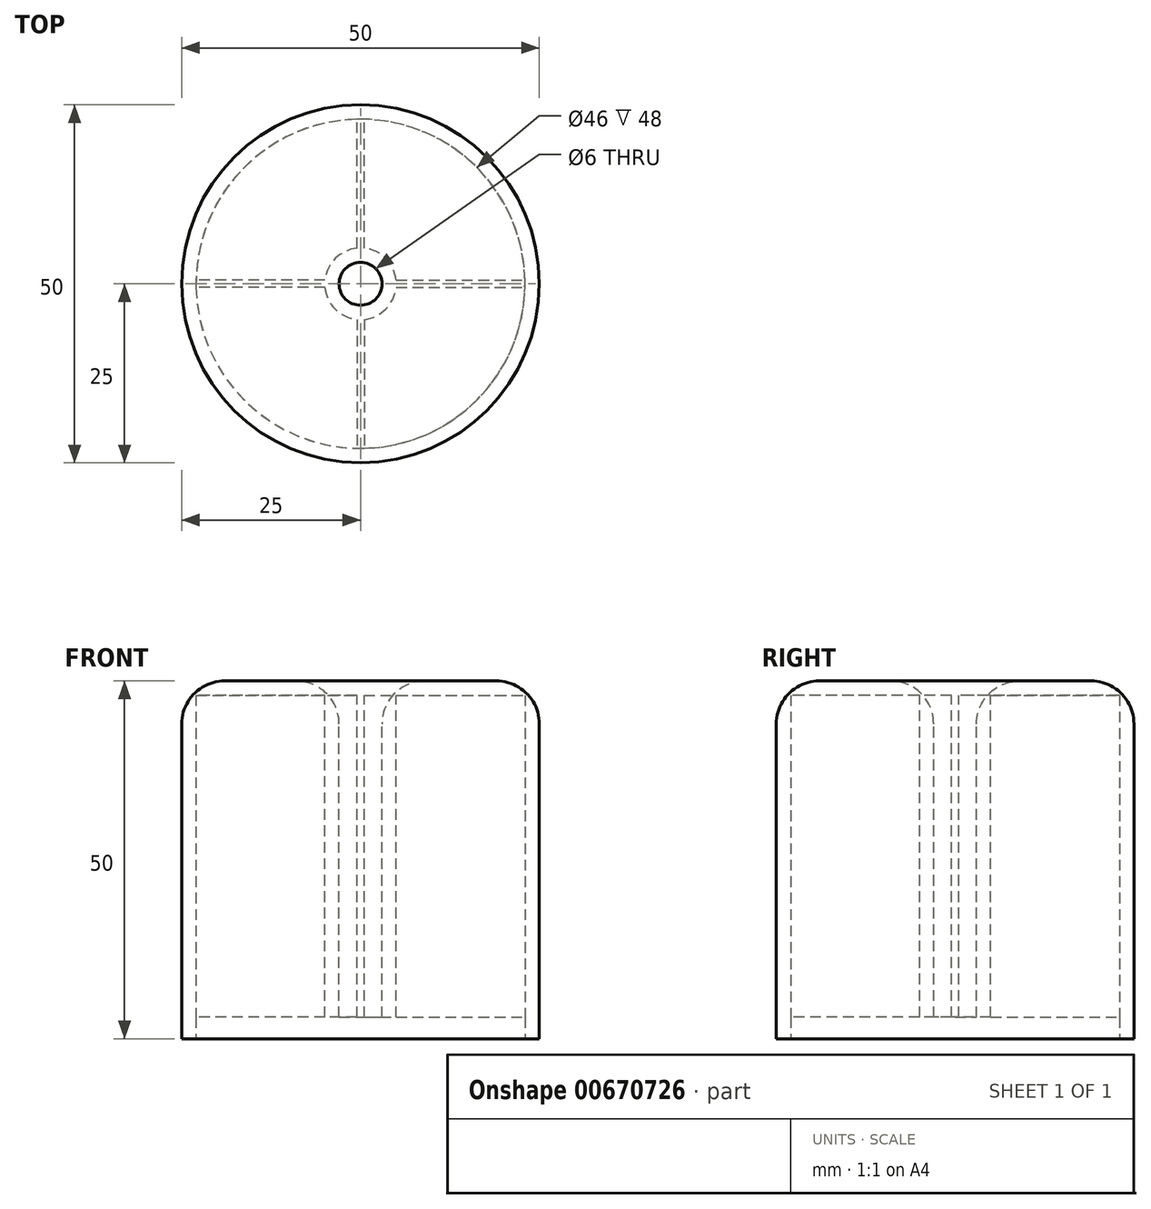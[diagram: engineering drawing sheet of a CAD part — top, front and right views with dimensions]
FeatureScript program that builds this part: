
annotation { "Feature Type Name" : "Feature", "Feature Type Description" : "" }
export const myFeature = defineFeature(function(context is Context, id is Id, definition is map)
    precondition{}
    {
        {
            var Q0;
            Q0=qCreatedBy(makeId("Top.planeOp"),FACE);
            var sketch = newSketch(context, id + "F0", { "sketchPlane" : qUnion([Q0])});
            skCircle(sketch, "E0", {"center": v(0, 0) * mm, "radius": 25 * mm});
            skSolve(sketch);
        }
        {
            var Q0;
            Q0 = qSketchRegion(id + "F0", true);
            extrude(context, id + "F1", {"entities" : qUnion([Q0]), "depth" : 50 * mm, "offsetDistance" : 25 * mm});
        }
        {
            var Q0;
            Q0=makeQuery(id+"F1.opExtrude","CAP_FACE",FACE,{"disambiguationData":[OSD([sQuery(id+"F0.wireOp",EDGE,"E0")])],"isStart":false});
            var sketch = newSketch(context, id + "F2", { "sketchPlane" : qUnion([Q0])});
            skCircle(sketch, "E1", {"center": v(0, 0) * mm, "radius": 3 * mm});
            skSolve(sketch);
        }
        {
            var Q0;
            Q0 = qSketchRegion(id + "F2", true);
            extrude(context, id + "F3", {"entities" : qUnion([Q0]), "operationType" : NewBodyOperationType.REMOVE, "oppositeDirection" : true, "depth" : 48 * mm, "offsetDistance" : 25 * mm});
        }
        {
            var Q0;
            Q0=makeQuery(id+"F1.opExtrude","CAP_FACE",FACE,{"disambiguationData":[OSD([sQuery(id+"F0.wireOp",EDGE,"E0")])],"isStart":true});
            shell(context, id + "F4", {"entities" : qUnion([Q0]), "thickness" : 2 * mm});
        }
        {
            var Q0;
            {var subQ0=sQuery(id+"F2.wireOp",EDGE,"E1");Q0=makeQuery(id+"F4.opShell","OFFSET_FACE",FACE,{"disambiguationData":[OSD([subQ0]),TDD([makeQuery(id+"F3.boolean.opBoolean","COPY",FACE,{"derivedFrom":makeQuery(id+"F3.opExtrude","CAP_FACE",FACE,{"disambiguationData":[OSD([subQ0])],"isStart":false})})])]});}
            var sketch = newSketch(context, id + "F5", { "sketchPlane" : qUnion([Q0])});
            skCircle(sketch, "E2.0", {"center": v(0, 0) * mm, "radius": 5 * mm});
            skSolve(sketch);
        }
        {
            var Q0;
            Q0 = qSketchRegion(id + "F5", true);
            extrude(context, id + "F6", {"entities" : qUnion([Q0]), "operationType" : NewBodyOperationType.REMOVE, "oppositeDirection" : true, "depth" : 3 * mm, "offsetDistance" : 25 * mm});
        }
        {
            var Q0;
            Q0=makeQuery(id+"F1.opExtrude","CAP_FACE",FACE,{"disambiguationData":[OSD([sQuery(id+"F0.wireOp",EDGE,"E0")])],"isStart":false});
            fillet(context, id + "F7", {"entities" : qUnion([Q0]), "radius" : 6 * mm, "tangentPropagation" : true, "allowEdgeOverflow" : false});
        }
        {
            var Q0;
            Q0=makeQuery(id+"F6.boolean.opBoolean","COPY",FACE,{"derivedFrom":makeQuery(id+"F6.opExtrude","CAP_FACE",FACE,{"disambiguationData":[OSD([sQuery(id+"F5.wireOp",EDGE,"E2.0")])],"isStart":false})});
            var sketch = newSketch(context, id + "F8", { "sketchPlane" : qUnion([Q0])});
            skLineSegment(sketch, "E3", {"start": v(0, 0) * mm, "end": v(25.2, 0) * mm, "construction": true});
            skLineSegment(sketch, "E4.0", {"start": v(3.98, -0.5) * mm, "end": v(23.8, -0.5) * mm});
            skLineSegment(sketch, "E5.0", {"start": v(3.98, 0.5) * mm, "end": v(23.8, 0.5) * mm});
            skLineSegment(sketch, "E6", {"start": v(3.98, 0.5) * mm, "end": v(3.98, -0.5) * mm});
            skLineSegment(sketch, "E7", {"start": v(23.8, 0.5) * mm, "end": v(23.8, -0.5) * mm});
            skPoint(sketch, "E8.orphan", {"position": v(25.2, -0.5) * mm});
            skSolve(sketch);
        }
        {
            var Q0;
            Q0 = qSketchRegion(id + "F8", true);
            extrude(context, id + "F9", {"entities" : qUnion([Q0]), "operationType" : NewBodyOperationType.ADD, "endBound" : BoundingType.UP_TO_NEXT, "oppositeDirection" : true, "depth" : 25 * mm, "offsetDistance" : 25 * mm});
        }
        {
            var Q0;
            Q0=makeQuery(id+"F1.opExtrude","SWEPT_BODY",BODY,{"disambiguationData":[OSD([sQuery(id+"F0.wireOp",EDGE,"E0")])]});
            var Q1;
            Q1=makeQuery(id+"F3.boolean.opBoolean","COPY",FACE,{"derivedFrom":makeQuery(id+"F3.opExtrude","SWEPT_FACE",FACE,{"disambiguationData":[OSD([sQuery(id+"F2.wireOp",EDGE,"E1")])]})});
            circularPattern(context, id + "F10", {"operationType" : NewBodyOperationType.ADD, "entities" : qUnion([Q0]), "axis" : qUnion([Q1]), "angle" : 360 * degree, "instanceCount" : 4, "equalSpace" : true});
        }
    });
